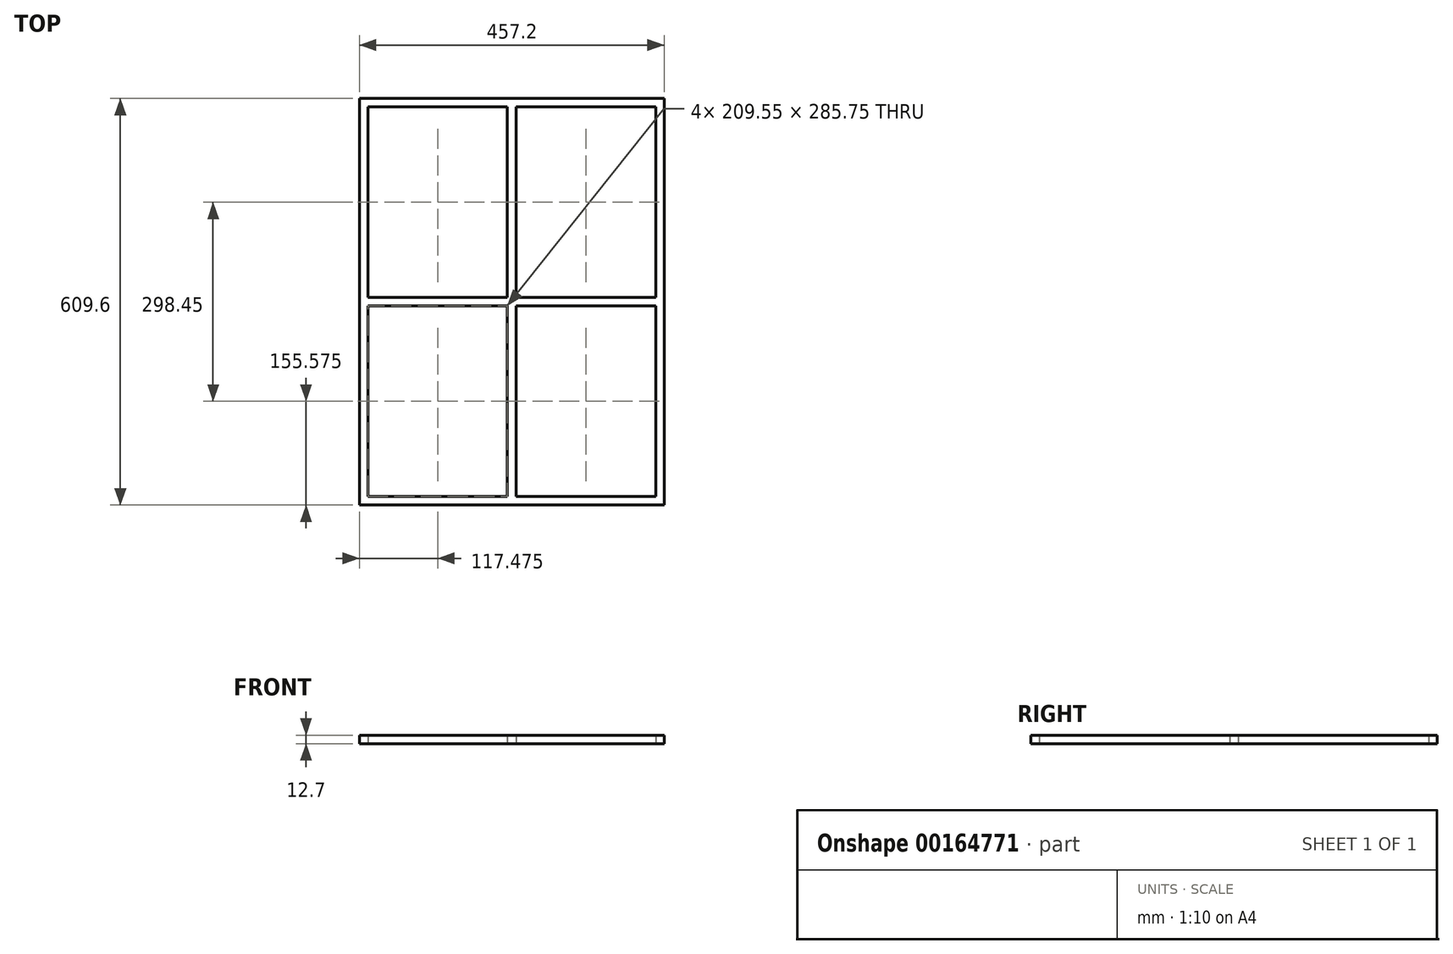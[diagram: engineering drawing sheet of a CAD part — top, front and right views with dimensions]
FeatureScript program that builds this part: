
annotation { "Feature Type Name" : "Feature", "Feature Type Description" : "" }
export const myFeature = defineFeature(function(context is Context, id is Id, definition is map)
    precondition{}
    {
        {
            var Q0;
            Q0=qCreatedBy(makeId("Top.planeOp"),FACE);
            var sketch = newSketch(context, id + "F0", { "sketchPlane" : qUnion([Q0])});
            skLineSegment(sketch, "E0.bottom", {"start": v(228.6, 304.8) * mm, "end": v(-228.6, 304.8) * mm});
            skLineSegment(sketch, "E0.top", {"start": v(228.6, -304.8) * mm, "end": v(-228.6, -304.8) * mm});
            skLineSegment(sketch, "E0.left", {"start": v(228.6, 304.8) * mm, "end": v(228.6, -304.8) * mm});
            skLineSegment(sketch, "E0.right", {"start": v(-228.6, 304.8) * mm, "end": v(-228.6, -304.8) * mm});
            skPoint(sketch, "E0.middle", {"position": v(0, 0) * mm});
            skLineSegment(sketch, "E1.bottom", {"start": v(6.35, 6.35) * mm, "end": v(-6.35, 6.35) * mm, "construction": true});
            skLineSegment(sketch, "E1.top", {"start": v(6.35, -6.35) * mm, "end": v(-6.35, -6.35) * mm, "construction": true});
            skLineSegment(sketch, "E1.left", {"start": v(6.35, 6.35) * mm, "end": v(6.35, -6.35) * mm, "construction": true});
            skLineSegment(sketch, "E1.right", {"start": v(-6.35, 6.35) * mm, "end": v(-6.35, -6.35) * mm, "construction": true});
            skLineSegment(sketch, "E2.bottom", {"start": v(6.35, 6.35) * mm, "end": v(215.9, 6.35) * mm});
            skLineSegment(sketch, "E2.top", {"start": v(6.35, 292.1) * mm, "end": v(215.9, 292.1) * mm});
            skLineSegment(sketch, "E2.left", {"start": v(6.35, 6.35) * mm, "end": v(6.35, 292.1) * mm});
            skLineSegment(sketch, "E2.right", {"start": v(215.9, 6.35) * mm, "end": v(215.9, 292.1) * mm});
            skLineSegment(sketch, "E3.bottom", {"start": v(-6.35, 6.35) * mm, "end": v(-215.9, 6.35) * mm});
            skLineSegment(sketch, "E3.top", {"start": v(-6.35, 292.1) * mm, "end": v(-215.9, 292.1) * mm});
            skLineSegment(sketch, "E3.left", {"start": v(-6.35, 6.35) * mm, "end": v(-6.35, 292.1) * mm});
            skLineSegment(sketch, "E3.right", {"start": v(-215.9, 6.35) * mm, "end": v(-215.9, 292.1) * mm});
            skLineSegment(sketch, "E4.bottom", {"start": v(-6.35, -6.35) * mm, "end": v(-215.9, -6.35) * mm});
            skLineSegment(sketch, "E4.top", {"start": v(-6.35, -292.1) * mm, "end": v(-215.9, -292.1) * mm});
            skLineSegment(sketch, "E4.left", {"start": v(-6.35, -6.35) * mm, "end": v(-6.35, -292.1) * mm});
            skLineSegment(sketch, "E4.right", {"start": v(-215.9, -6.35) * mm, "end": v(-215.9, -292.1) * mm});
            skLineSegment(sketch, "E5.bottom", {"start": v(6.35, -6.35) * mm, "end": v(215.9, -6.35) * mm});
            skLineSegment(sketch, "E5.top", {"start": v(6.35, -292.1) * mm, "end": v(215.9, -292.1) * mm});
            skLineSegment(sketch, "E5.left", {"start": v(6.35, -6.35) * mm, "end": v(6.35, -292.1) * mm});
            skLineSegment(sketch, "E5.right", {"start": v(215.9, -6.35) * mm, "end": v(215.9, -292.1) * mm});
            skLineSegment(sketch, "E6", {"start": v(-215.9, 292.1) * mm, "end": v(-228.6, 292.1) * mm, "construction": true});
            skLineSegment(sketch, "E7", {"start": v(-215.9, 292.1) * mm, "end": v(-215.9, 304.8) * mm, "construction": true});
            skSolve(sketch);
        }
        {
            var Q0;
            Q0=qSketchRegion(id+"F0",true);
            extrude(context, id + "F1", {"entities" : qUnion([Q0]), "depth" : 12.7 * mm});
        }
    });
